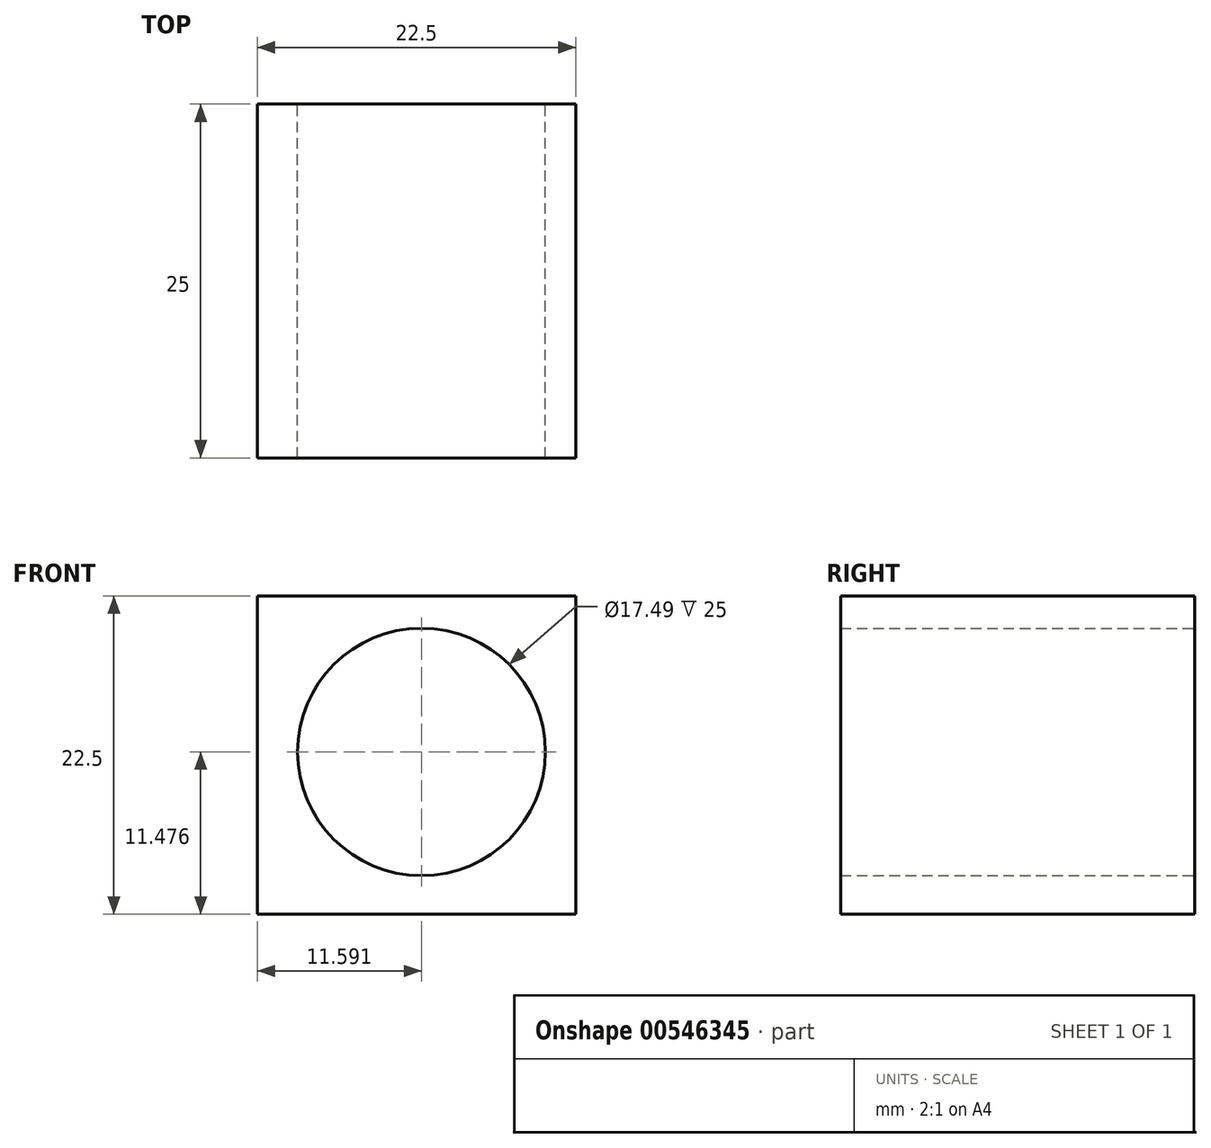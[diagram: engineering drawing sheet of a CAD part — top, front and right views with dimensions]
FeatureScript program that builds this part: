
annotation { "Feature Type Name" : "Feature", "Feature Type Description" : "" }
export const myFeature = defineFeature(function(context is Context, id is Id, definition is map)
    precondition{}
    {
        {
            var Q0;
            Q0=qCreatedBy(makeId("Front.planeOp"),FACE);
            var sketch = newSketch(context, id + "F0", { "sketchPlane" : qUnion([Q0])});
            skLineSegment(sketch, "E0.bottom", {"start": v(0, 0) * mm, "end": v(-22.5, 0) * mm});
            skLineSegment(sketch, "E0.top", {"start": v(0, 22.5) * mm, "end": v(-22.5, 22.5) * mm});
            skLineSegment(sketch, "E0.left", {"start": v(0, 0) * mm, "end": v(0, 22.5) * mm});
            skLineSegment(sketch, "E0.right", {"start": v(-22.5, 0) * mm, "end": v(-22.5, 22.5) * mm});
            skCircle(sketch, "E1", {"center": v(-10.9, 11.48) * mm, "radius": 8.74 * mm});
            skSolve(sketch);
        }
        {
            var Q0;
            Q0 = qSketchRegion(id + "F0", true);
            extrude(context, id + "F1", {"entities" : qUnion([Q0]), "depth" : 25 * mm, "offsetDistance" : 25 * mm});
        }
    });
